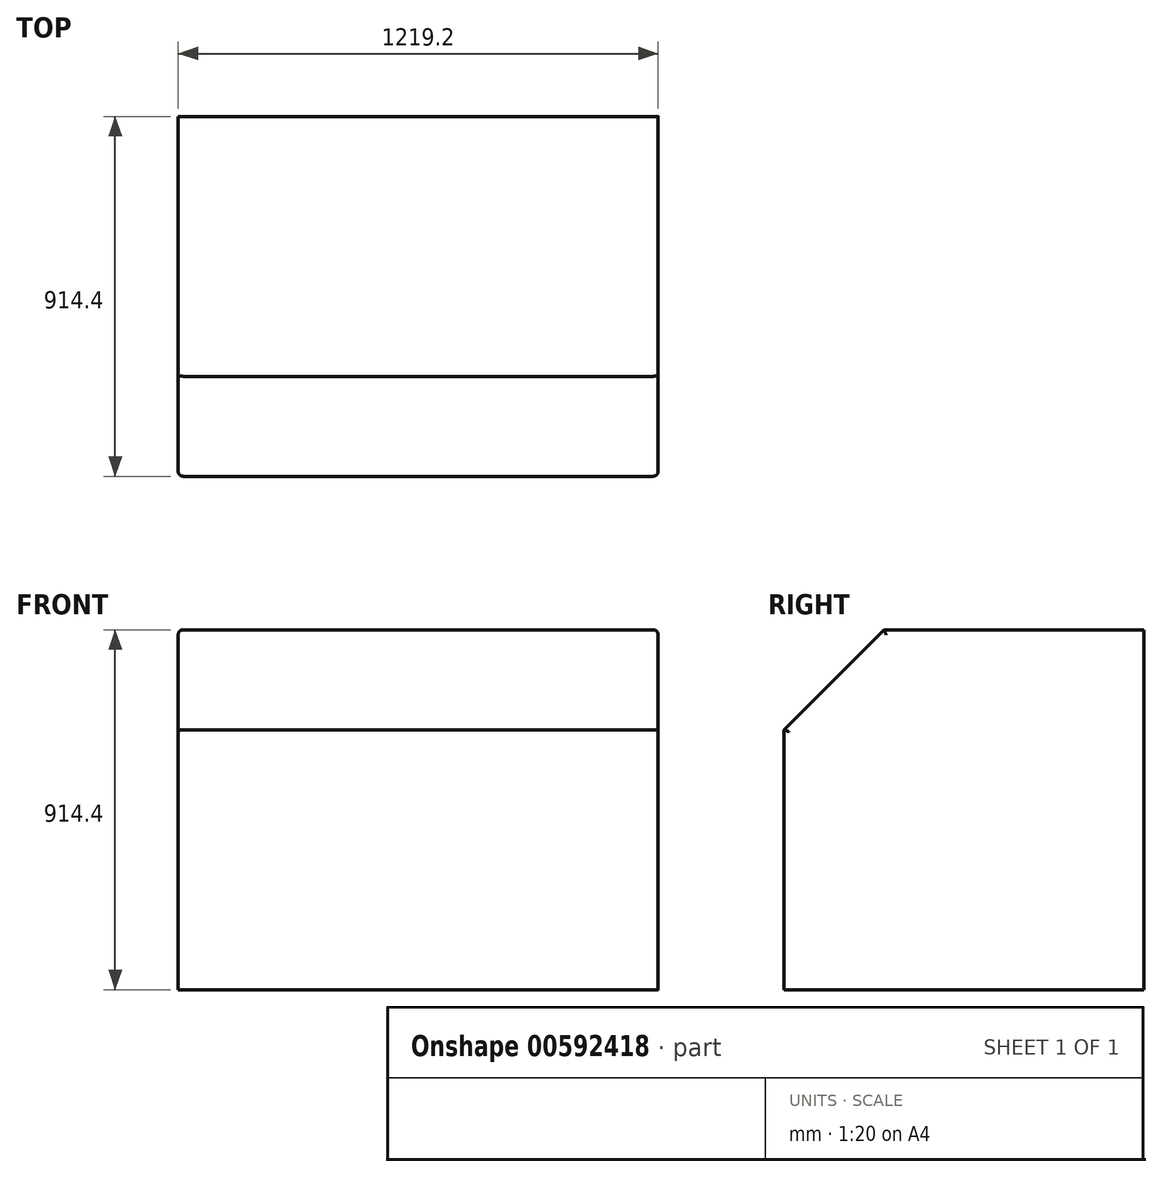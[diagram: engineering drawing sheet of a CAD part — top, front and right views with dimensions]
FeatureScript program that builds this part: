
annotation { "Feature Type Name" : "Feature", "Feature Type Description" : "" }
export const myFeature = defineFeature(function(context is Context, id is Id, definition is map)
    precondition{}
    {
        {
            var Q0;
            Q0=qCreatedBy(makeId("Top.planeOp"),FACE);
            var sketch = newSketch(context, id + "F0", { "sketchPlane" : qUnion([Q0])});
            skLineSegment(sketch, "E0.bottom", {"start": v(609.6, -457.2) * mm, "end": v(-609.6, -457.2) * mm});
            skLineSegment(sketch, "E0.top", {"start": v(609.6, 457.2) * mm, "end": v(-609.6, 457.2) * mm});
            skLineSegment(sketch, "E0.left", {"start": v(609.6, -457.2) * mm, "end": v(609.6, 457.2) * mm});
            skLineSegment(sketch, "E0.right", {"start": v(-609.6, -457.2) * mm, "end": v(-609.6, 457.2) * mm});
            skPoint(sketch, "E0.middle", {"position": v(0, 0) * mm});
            skSolve(sketch);
        }
        {
            var Q0;
            Q0=makeQuery(id+"F0.imprint","IMPRINT",FACE,{"disambiguationData":[TD([[makeQuery(id+"F0.imprint","IMPRINT",EDGE,{"derivedFrom":sQuery(id+"F0.wireOp",EDGE,"E0.bottom")}),-1.0]])]});
            extrude(context, id + "F1", {"entities" : qUnion([Q0]), "depth" : 914.4 * mm, "offsetDistance" : 25.4 * mm});
        }
        {
            var Q0;
            Q0=makeQuery(id+"F1.opExtrude","CAP_EDGE",EDGE,{"disambiguationData":[OSD([sQuery(id+"F0.wireOp",EDGE,"E0.bottom")])],"isStart":false});
            chamfer(context, id + "F2", {"entities" : qUnion([Q0]), "width" : 254 * mm, "tangentPropagation" : true});
        }
        {
            var Q0;
            Q0=makeQuery(id+"F1.opExtrude","CAP_EDGE",EDGE,{"disambiguationData":[OSD([sQuery(id+"F0.wireOp",EDGE,"E0.left")])],"isStart":false});
            var Q1;
            Q1=makeQuery(id+"F2.opChamfer","BLEND_EDGE",EDGE,{"blendedFrom":[makeQuery(id+"F1.opExtrude","CAP_EDGE",EDGE,{"disambiguationData":[OSD([sQuery(id+"F0.wireOp",EDGE,"E0.bottom")])],"isStart":false}),makeQuery(id+"F1.opExtrude","SWEPT_FACE",FACE,{"disambiguationData":[OSD([sQuery(id+"F0.wireOp",EDGE,"E0.left")])]})],"blendedInto":[makeQuery(id+"F1.opExtrude","SWEPT_FACE",FACE,{"disambiguationData":[OSD([sQuery(id+"F0.wireOp",EDGE,"E0.left")])]})]});
            var Q2;
            Q2=makeQuery(id+"F1.opExtrude","SWEPT_EDGE",EDGE,{"disambiguationData":[OSD([sQuery(id+"F0.wireOp",EDGE,"E0.bottom"),sQuery(id+"F0.wireOp",EDGE,"E0.left")])]});
            var Q3;
            Q3=makeQuery(id+"F1.opExtrude","SWEPT_EDGE",EDGE,{"disambiguationData":[OSD([sQuery(id+"F0.wireOp",EDGE,"E0.bottom"),sQuery(id+"F0.wireOp",EDGE,"E0.right")])]});
            var Q4;
            Q4=makeQuery(id+"F2.opChamfer","BLEND_EDGE",EDGE,{"blendedFrom":[makeQuery(id+"F1.opExtrude","CAP_EDGE",EDGE,{"disambiguationData":[OSD([sQuery(id+"F0.wireOp",EDGE,"E0.bottom")])],"isStart":false}),makeQuery(id+"F1.opExtrude","SWEPT_FACE",FACE,{"disambiguationData":[OSD([sQuery(id+"F0.wireOp",EDGE,"E0.right")])]})],"blendedInto":[makeQuery(id+"F1.opExtrude","SWEPT_FACE",FACE,{"disambiguationData":[OSD([sQuery(id+"F0.wireOp",EDGE,"E0.right")])]})]});
            var Q5;
            Q5=makeQuery(id+"F1.opExtrude","CAP_EDGE",EDGE,{"disambiguationData":[OSD([sQuery(id+"F0.wireOp",EDGE,"E0.right")])],"isStart":false});
            fillet(context, id + "F3", {"entities" : qUnion([Q0, Q1, Q2, Q3, Q4, Q5]), "radius" : 12.7 * mm, "tangentPropagation" : true, "allowEdgeOverflow" : false});
        }
    });
